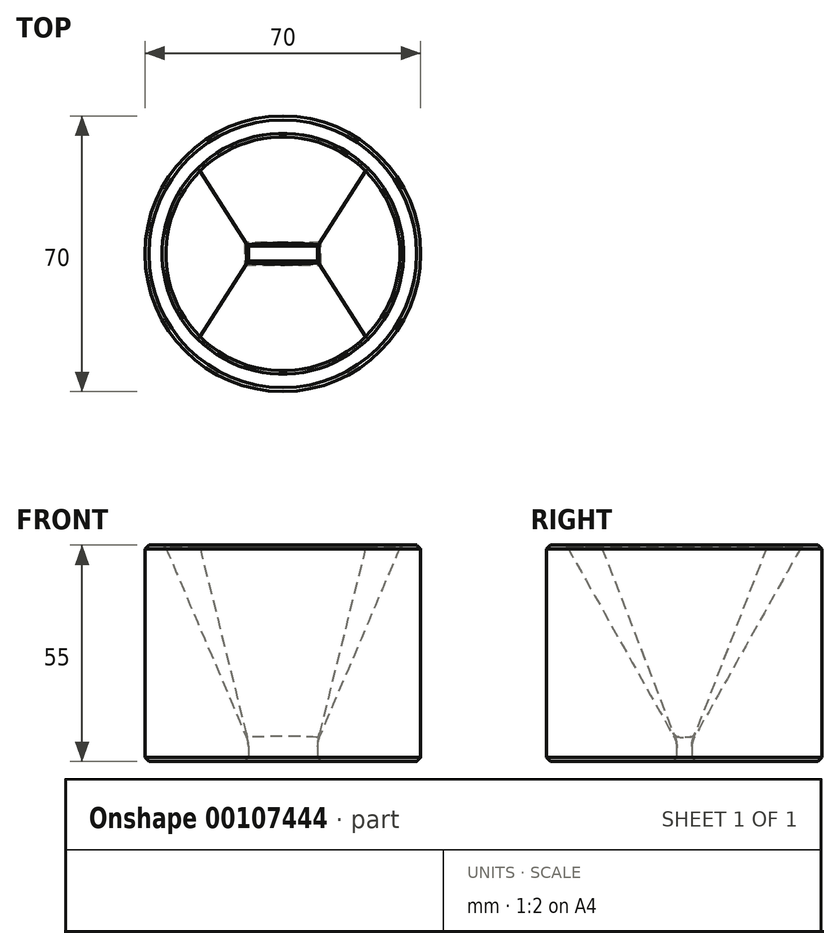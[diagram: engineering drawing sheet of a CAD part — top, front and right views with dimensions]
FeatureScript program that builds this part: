
annotation { "Feature Type Name" : "Feature", "Feature Type Description" : "" }
export const myFeature = defineFeature(function(context is Context, id is Id, definition is map)
    precondition{}
    {
        {
            var Q0;
            Q0=qCreatedBy(makeId("Top.planeOp"),FACE);
            var sketch = newSketch(context, id + "F0", { "sketchPlane" : qUnion([Q0])});
            skLineSegment(sketch, "E0.bottom", {"start": v(8.76, -1.9) * mm, "end": v(-8.76, -1.9) * mm});
            skLineSegment(sketch, "E0.top", {"start": v(8.76, 1.9) * mm, "end": v(-8.76, 1.9) * mm});
            skLineSegment(sketch, "E0.left", {"start": v(8.76, -1.9) * mm, "end": v(8.76, 1.9) * mm});
            skLineSegment(sketch, "E0.right", {"start": v(-8.76, -1.9) * mm, "end": v(-8.76, 1.9) * mm});
            skPoint(sketch, "E0.middle", {"position": v(0, 0) * mm});
            skLineSegment(sketch, "E1.0", {"start": v(13.76, 6.9) * mm, "end": v(-13.76, 6.9) * mm});
            skLineSegment(sketch, "E1.1", {"start": v(13.76, -6.9) * mm, "end": v(13.76, 6.9) * mm});
            skLineSegment(sketch, "E1.2", {"start": v(13.76, -6.9) * mm, "end": v(-13.76, -6.9) * mm});
            skLineSegment(sketch, "E1.3", {"start": v(-13.76, -6.9) * mm, "end": v(-13.76, 6.9) * mm});
            skSolve(sketch);
        }
        {
            var Q0;
            Q0=qCreatedBy(makeId("Top.planeOp"),FACE);
            cPlane(context, id + "F1", {"entities" : qUnion([Q0]), "cplaneType" : CPlaneType.OFFSET, "offset" : 50 * mm, "width" : 150 * mm, "height" : 150 * mm});
        }
        {
            var Q0;
            Q0=qCreatedBy(id+"F1.planeOp",FACE);
            var sketch = newSketch(context, id + "F2", { "sketchPlane" : qUnion([Q0])});
            skPoint(sketch, "E2.middle", {"position": v(0, 0) * mm});
            skArc(sketch, "E3", {"start": v(-24.75, 24.75) * mm, "mid": v(-35, 0) * mm, "end": v(-24.75, -24.75) * mm});
            skArc(sketch, "E4", {"start": v(24.75, 24.75) * mm, "mid": v(0, 35) * mm, "end": v(-24.75, 24.75) * mm});
            skArc(sketch, "E5", {"start": v(-24.75, -24.75) * mm, "mid": v(0, -35) * mm, "end": v(24.75, -24.75) * mm});
            skArc(sketch, "E6", {"start": v(-21.21, 21.21) * mm, "mid": v(-30, 0) * mm, "end": v(-21.21, -21.21) * mm});
            skArc(sketch, "E7", {"start": v(21.21, 21.21) * mm, "mid": v(0, 30) * mm, "end": v(-21.21, 21.21) * mm});
            skArc(sketch, "E8", {"start": v(21.21, -21.21) * mm, "mid": v(30, 0) * mm, "end": v(21.21, 21.21) * mm});
            skArc(sketch, "E9", {"start": v(-21.21, -21.21) * mm, "mid": v(0, -30) * mm, "end": v(21.21, -21.21) * mm});
            skArc(sketch, "E10", {"start": v(24.75, -24.75) * mm, "mid": v(35, 0) * mm, "end": v(24.75, 24.75) * mm});
            skSolve(sketch);
        }
        {
            var Q0;
            Q0=makeQuery(id+"F2.imprint","IMPRINT",FACE,{"disambiguationData":[TD([[makeQuery(id+"F2.imprint","IMPRINT",EDGE,{"derivedFrom":sQuery(id+"F2.wireOp",EDGE,"E6")}),1.0]])]});
            var Q1;
            Q1=makeQuery(id+"F0.imprint","IMPRINT",FACE,{"disambiguationData":[TD([[makeQuery(id+"F0.imprint","IMPRINT",EDGE,{"derivedFrom":sQuery(id+"F0.wireOp",EDGE,"E0.bottom")}),-1.0]])]});
            loft(context, id + "F3", {"sheetProfilesArray" : [{ "sheetProfileEntities" : qUnion([Q0]) }, { "sheetProfileEntities" : qUnion([Q1]) }]});
        }
        {
            var Q0;
            Q0=makeQuery(id+"F2.imprint","IMPRINT",FACE,{"disambiguationData":[TD([[makeQuery(id+"F2.imprint","IMPRINT",EDGE,{"derivedFrom":sQuery(id+"F2.wireOp",EDGE,"E6")}),1.0]])]});
            var sketch = newSketch(context, id + "F4", { "sketchPlane" : qUnion([Q0])});
            skArc(sketch, "E11.0", {"start": v(-24.75, 24.75) * mm, "mid": v(-35, 0) * mm, "end": v(-24.75, -24.75) * mm});
            skArc(sketch, "E12.0", {"start": v(-24.75, -24.75) * mm, "mid": v(0, -35) * mm, "end": v(24.75, -24.75) * mm});
            skArc(sketch, "E13.0", {"start": v(24.75, -24.75) * mm, "mid": v(35, 0) * mm, "end": v(24.75, 24.75) * mm});
            skArc(sketch, "E14.0", {"start": v(24.75, 24.75) * mm, "mid": v(0, 35) * mm, "end": v(-24.75, 24.75) * mm});
            skSolve(sketch);
        }
        {
            var Q0;
            Q0=makeQuery(id+"F4.imprint","IMPRINT",FACE,{"disambiguationData":[TD([[makeQuery(id+"F4.imprint","IMPRINT",EDGE,{"derivedFrom":sQuery(id+"F4.wireOp",EDGE,"E11.0")}),1.0]])]});
            var Q1;
            Q1=makeQuery(id+"F4.imprint","IMPRINT",FACE,{"disambiguationData":[TD([[makeQuery(id+"F4.imprint","IMPRINT",EDGE,{"derivedFrom":makeQuery(id+"F2.imprint","IMPRINT",EDGE,{"derivedFrom":sQuery(id+"F2.wireOp",EDGE,"E6")})}),1.0]])]});
            extrude(context, id + "F5", {"entities" : qUnion([Q0, Q1]), "oppositeDirection" : true, "depth" : 50 * mm});
        }
        {
            var Q0;
            Q0=makeQuery(id+"F3.opLoft","SWEPT_BODY",BODY,{"disambiguationData":[OSD([makeQuery(id+"F0.imprint","IMPRINT",FACE,{"disambiguationData":[TD([[makeQuery(id+"F0.imprint","IMPRINT",EDGE,{"derivedFrom":sQuery(id+"F0.wireOp",EDGE,"E0.bottom")}),-1.0]])]}),makeQuery(id+"F2.imprint","IMPRINT",FACE,{"disambiguationData":[TD([[makeQuery(id+"F2.imprint","IMPRINT",EDGE,{"derivedFrom":sQuery(id+"F2.wireOp",EDGE,"E6")}),1.0]])]})])]});
            var Q1;
            Q1=makeQuery(id+"F5.opExtrude","SWEPT_BODY",BODY,{"disambiguationData":[OSD([sQuery(id+"F4.wireOp",EDGE,"E11.0"),sQuery(id+"F4.wireOp",EDGE,"E12.0"),sQuery(id+"F4.wireOp",EDGE,"E13.0"),sQuery(id+"F4.wireOp",EDGE,"E14.0")])]});
            booleanBodies(context, id + "F6", {"operationType" : BooleanOperationType.SUBTRACTION, "tools" : qUnion([Q0]), "targets" : qUnion([Q1])});
        }
        {
            var Q0;
            Q0=makeQuery(id+"F5.opExtrude","CAP_FACE",FACE,{"disambiguationData":[OSD([sQuery(id+"F4.wireOp",EDGE,"E11.0"),sQuery(id+"F4.wireOp",EDGE,"E12.0"),sQuery(id+"F4.wireOp",EDGE,"E13.0"),sQuery(id+"F4.wireOp",EDGE,"E14.0")])],"isStart":false});
            extrude(context, id + "F7", {"entities" : qUnion([Q0]), "operationType" : NewBodyOperationType.ADD, "depth" : 5 * mm});
        }
        {
            var Q0;
            Q0=makeQuery(id+"F7.opExtrude","CAP_FACE",FACE,{"disambiguationData":[OSD([sQuery(id+"F4.wireOp",EDGE,"E11.0"),sQuery(id+"F4.wireOp",EDGE,"E12.0"),sQuery(id+"F4.wireOp",EDGE,"E13.0"),sQuery(id+"F4.wireOp",EDGE,"E14.0")])],"isStart":false});
            var Q1;
            Q1=makeQuery(id+"F5.opExtrude","CAP_FACE",FACE,{"disambiguationData":[OSD([sQuery(id+"F4.wireOp",EDGE,"E11.0"),sQuery(id+"F4.wireOp",EDGE,"E12.0"),sQuery(id+"F4.wireOp",EDGE,"E13.0"),sQuery(id+"F4.wireOp",EDGE,"E14.0")])],"isStart":true});
            chamfer(context, id + "F8", {"entities" : qUnion([Q0, Q1]), "width" : 1 * mm, "tangentPropagation" : true});
        }
        {
            var Q0;
            {var subQ0=sQuery(id+"F0.wireOp",EDGE,"E0.right");var subQ1=sQuery(id+"F0.wireOp",EDGE,"E0.left");var subQ2=sQuery(id+"F0.wireOp",EDGE,"E0.top");Q0=makeQuery(id+"F7.boolean.opBoolean","MERGE",EDGE,{"derivedFrom":[makeQuery(id+"F6.opBoolean","COPY",EDGE,{"derivedFrom":makeQuery(id+"F3.opLoft","MID_CAP_EDGE",EDGE,{"disambiguationData":[OSD([subQ2,subQ1,subQ0])],"capPos":1.0})}),makeQuery(id+"F7.opExtrude","CAP_EDGE",EDGE,{"disambiguationData":[OSD([subQ2,subQ1,subQ0])],"isStart":true})]});}
            var Q1;
            {var subQ0=sQuery(id+"F0.wireOp",EDGE,"E0.left");var subQ1=sQuery(id+"F0.wireOp",EDGE,"E0.top");var subQ2=sQuery(id+"F0.wireOp",EDGE,"E0.bottom");Q1=makeQuery(id+"F7.boolean.opBoolean","MERGE",EDGE,{"derivedFrom":[makeQuery(id+"F6.opBoolean","COPY",EDGE,{"derivedFrom":makeQuery(id+"F3.opLoft","MID_CAP_EDGE",EDGE,{"disambiguationData":[OSD([subQ2,subQ1,subQ0])],"capPos":1.0})}),makeQuery(id+"F7.opExtrude","CAP_EDGE",EDGE,{"disambiguationData":[OSD([subQ2,subQ1,subQ0])],"isStart":true})]});}
            var Q2;
            {var subQ0=sQuery(id+"F0.wireOp",EDGE,"E0.right");var subQ1=sQuery(id+"F0.wireOp",EDGE,"E0.left");var subQ2=sQuery(id+"F0.wireOp",EDGE,"E0.bottom");Q2=makeQuery(id+"F7.boolean.opBoolean","MERGE",EDGE,{"derivedFrom":[makeQuery(id+"F6.opBoolean","COPY",EDGE,{"derivedFrom":makeQuery(id+"F3.opLoft","MID_CAP_EDGE",EDGE,{"disambiguationData":[OSD([subQ2,subQ1,subQ0])],"capPos":1.0})}),makeQuery(id+"F7.opExtrude","CAP_EDGE",EDGE,{"disambiguationData":[OSD([subQ2,subQ1,subQ0])],"isStart":true})]});}
            var Q3;
            {var subQ0=sQuery(id+"F0.wireOp",EDGE,"E0.right");var subQ1=sQuery(id+"F0.wireOp",EDGE,"E0.top");var subQ2=sQuery(id+"F0.wireOp",EDGE,"E0.bottom");Q3=makeQuery(id+"F7.boolean.opBoolean","MERGE",EDGE,{"derivedFrom":[makeQuery(id+"F6.opBoolean","COPY",EDGE,{"derivedFrom":makeQuery(id+"F3.opLoft","MID_CAP_EDGE",EDGE,{"disambiguationData":[OSD([subQ2,subQ1,subQ0])],"capPos":1.0})}),makeQuery(id+"F7.opExtrude","CAP_EDGE",EDGE,{"disambiguationData":[OSD([subQ2,subQ1,subQ0])],"isStart":true})]});}
            fillet(context, id + "F9", {"entities" : qUnion([Q0, Q1, Q2, Q3]), "radius" : 6 * mm, "tangentPropagation" : true, "rho" : 0.5, "crossSection" : FilletCrossSection.CONIC, "allowEdgeOverflow" : false});
        }
    });
